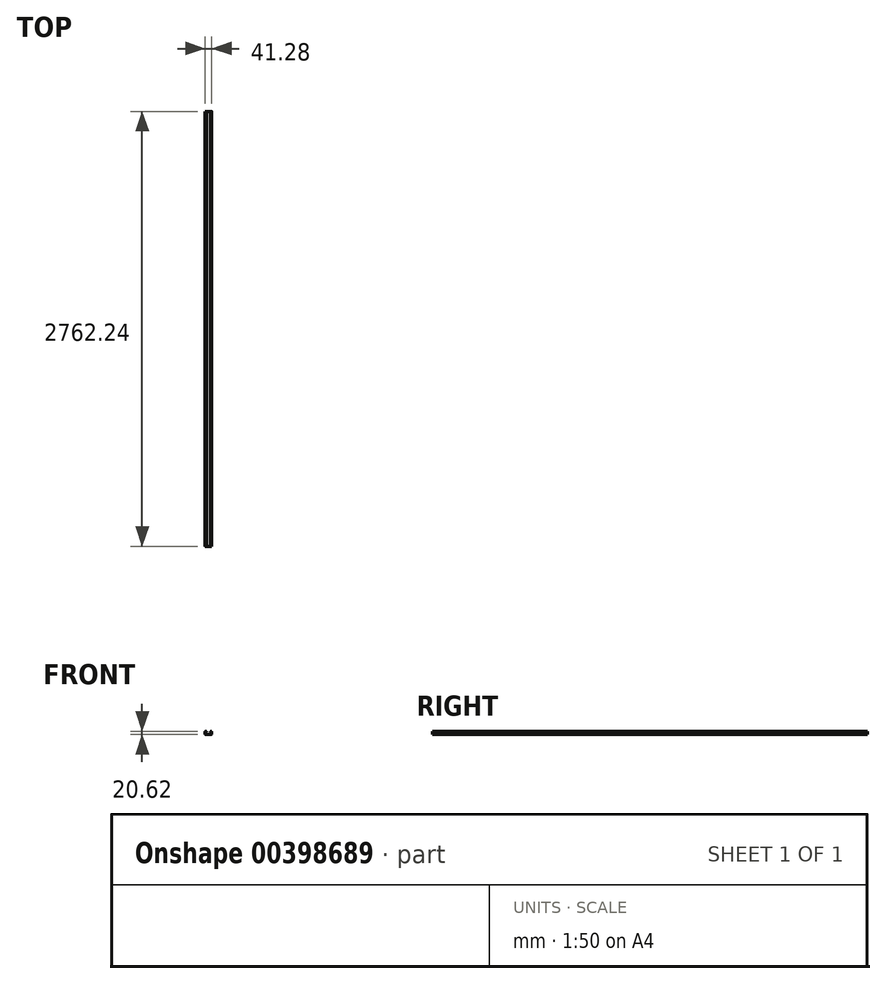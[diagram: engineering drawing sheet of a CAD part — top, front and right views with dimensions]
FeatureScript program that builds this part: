
annotation { "Feature Type Name" : "Feature", "Feature Type Description" : "" }
export const myFeature = defineFeature(function(context is Context, id is Id, definition is map)
    precondition{}
    {
        {
            var Q0;
            Q0=qCreatedBy(makeId("Front.planeOp"),FACE);
            var sketch = newSketch(context, id + "F0", { "sketchPlane" : qUnion([Q0])});
            skLineSegment(sketch, "E0.bottom", {"start": v(0, 0) * mm, "end": v(41.28, 0) * mm});
            skLineSegment(sketch, "E0.left", {"start": v(0, 0) * mm, "end": v(0, 16.66) * mm});
            skLineSegment(sketch, "E0.right", {"start": v(41.28, 0) * mm, "end": v(41.28, 16.66) * mm});
            skArc(sketch, "E1", {"start": v(7.92, 16.66) * mm, "mid": v(3.96, 20.62) * mm, "end": v(0, 16.66) * mm});
            skLineSegment(sketch, "E2.0", {"start": v(1.59, 1.59) * mm, "end": v(1.59, 16.66) * mm});
            skLineSegment(sketch, "E3.0", {"start": v(1.59, 1.59) * mm, "end": v(39.69, 1.59) * mm});
            skLineSegment(sketch, "E4.0", {"start": v(39.69, 1.59) * mm, "end": v(39.69, 16.66) * mm});
            skArc(sketch, "E5", {"start": v(6.34, 16.66) * mm, "mid": v(3.96, 19.04) * mm, "end": v(1.59, 16.66) * mm});
            skArc(sketch, "E6.MirrorC", {"start": v(33.35, 16.66) * mm, "mid": v(37.31, 20.62) * mm, "end": v(41.28, 16.66) * mm});
            skArc(sketch, "E7.MirrorC", {"start": v(34.94, 16.66) * mm, "mid": v(37.31, 19.04) * mm, "end": v(39.69, 16.66) * mm});
            skLineSegment(sketch, "E8.trimOffspring", {"start": v(33.35, 16.66) * mm, "end": v(34.94, 16.66) * mm});
            skLineSegment(sketch, "E9.trimOffspring", {"start": v(6.34, 16.66) * mm, "end": v(7.92, 16.66) * mm});
            skSolve(sketch);
        }
        {
            var Q0;
            Q0 = qSketchRegion(id + "F0", true);
            extrude(context, id + "F1", {"entities" : qUnion([Q0]), "endBound" : BoundingType.SYMMETRIC, "depth" : 2762.25 * mm});
        }
        {
            var Q0;
            Q0=makeQuery(id+"F1.opExtrude","SWEPT_EDGE",EDGE,{"disambiguationData":[OSD([sQuery(id+"F0.wireOp",EDGE,"E0.bottom"),sQuery(id+"F0.wireOp",EDGE,"E0.right")])]});
            var Q1;
            Q1=makeQuery(id+"F1.opExtrude","SWEPT_EDGE",EDGE,{"disambiguationData":[OSD([sQuery(id+"F0.wireOp",EDGE,"E0.bottom"),sQuery(id+"F0.wireOp",EDGE,"E0.left")])]});
            var Q2;
            Q2=makeQuery(id+"F1.opExtrude","SWEPT_EDGE",EDGE,{"disambiguationData":[OSD([sQuery(id+"F0.wireOp",EDGE,"E3.0"),sQuery(id+"F0.wireOp",EDGE,"E4.0")])]});
            var Q3;
            Q3=makeQuery(id+"F1.opExtrude","SWEPT_EDGE",EDGE,{"disambiguationData":[OSD([sQuery(id+"F0.wireOp",EDGE,"E2.0"),sQuery(id+"F0.wireOp",EDGE,"E3.0")])]});
            fillet(context, id + "F2", {"entities" : qUnion([Q0, Q1, Q2, Q3]), "radius" : 1.59 * mm, "tangentPropagation" : true, "allowEdgeOverflow" : false});
        }
        {
            var Q0;
            Q0=makeQuery(id+"F1.opExtrude","SWEPT_EDGE",EDGE,{"disambiguationData":[OSD([sQuery(id+"F0.wireOp",EDGE,"E1"),sQuery(id+"F0.wireOp",EDGE,"E9.trimOffspring")])]});
            var Q1;
            Q1=makeQuery(id+"F1.opExtrude","SWEPT_EDGE",EDGE,{"disambiguationData":[OSD([sQuery(id+"F0.wireOp",EDGE,"E5"),sQuery(id+"F0.wireOp",EDGE,"E9.trimOffspring")])]});
            var Q2;
            Q2=makeQuery(id+"F1.opExtrude","SWEPT_EDGE",EDGE,{"disambiguationData":[OSD([sQuery(id+"F0.wireOp",EDGE,"E6.MirrorC"),sQuery(id+"F0.wireOp",EDGE,"E8.trimOffspring")])]});
            var Q3;
            Q3=makeQuery(id+"F1.opExtrude","SWEPT_EDGE",EDGE,{"disambiguationData":[OSD([sQuery(id+"F0.wireOp",EDGE,"E7.MirrorC"),sQuery(id+"F0.wireOp",EDGE,"E8.trimOffspring")])]});
            fillet(context, id + "F3", {"entities" : qUnion([Q0, Q1, Q2, Q3]), "radius" : 0.83 * mm, "tangentPropagation" : true, "allowEdgeOverflow" : false});
        }
    });
